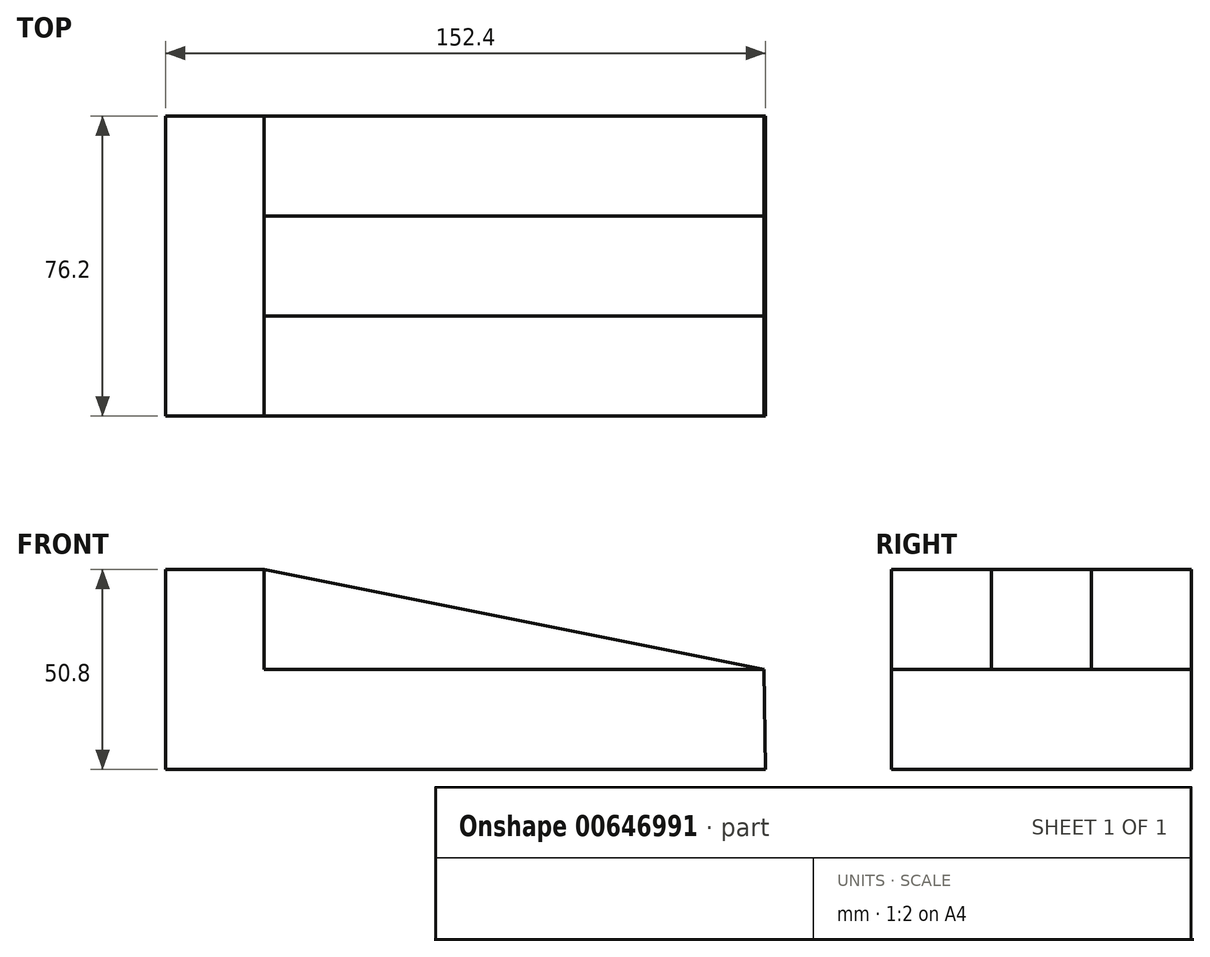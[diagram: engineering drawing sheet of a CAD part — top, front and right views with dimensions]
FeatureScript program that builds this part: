
annotation { "Feature Type Name" : "Feature", "Feature Type Description" : "" }
export const myFeature = defineFeature(function(context is Context, id is Id, definition is map)
    precondition{}
    {
        {
            var Q0;
            Q0=qCreatedBy(makeId("Front.planeOp"),FACE);
            var sketch = newSketch(context, id + "F0", { "sketchPlane" : qUnion([Q0])});
            skLineSegment(sketch, "E0", {"start": v(-56.03, 50.8) * mm, "end": v(-81.43, 50.8) * mm});
            skLineSegment(sketch, "E1", {"start": v(-81, 50.8) * mm, "end": v(-81, 0) * mm});
            skLineSegment(sketch, "E2", {"start": v(-81, 0) * mm, "end": v(71.4, 0) * mm});
            skLineSegment(sketch, "E3", {"start": v(71.4, 0) * mm, "end": v(70.97, 25.4) * mm});
            skLineSegment(sketch, "E4", {"start": v(70.97, 25.4) * mm, "end": v(-56.03, 25.4) * mm});
            skLineSegment(sketch, "E5", {"start": v(-56.03, 25.4) * mm, "end": v(-56.03, 50.8) * mm});
            skLineSegment(sketch, "E6", {"start": v(-56.03, 50.8) * mm, "end": v(70.97, 25.4) * mm});
            skSolve(sketch);
        }
        {
            var Q0;
            {var subQ0=sQuery(id+"F0.wireOp",EDGE,"E2");Q0=makeQuery(id+"F0.imprint","IMPRINT",FACE,{"disambiguationData":[TD([[makeQuery(id+"F0.imprint","IMPRINT",EDGE,{"derivedFrom":subQ0}),1.0]])]});}
            extrude(context, id + "F1", {"entities" : qUnion([Q0]), "depth" : 50.8 * mm, "offsetDistance" : 25.4 * mm, "hasSecondDirection" : true, "secondDirectionOppositeDirection" : true, "secondDirectionDepth" : 25.4 * mm});
        }
        {
            var Q0;
            Q0=makeQuery(id+"F0.imprint","IMPRINT",FACE,{"disambiguationData":[TD([[makeQuery(id+"F0.imprint","IMPRINT",EDGE,{"derivedFrom":sQuery(id+"F0.wireOp",EDGE,"E4")}),-1.0]])]});
            extrude(context, id + "F2", {"entities" : qUnion([Q0]), "operationType" : NewBodyOperationType.ADD, "depth" : 25.4 * mm, "offsetDistance" : 25.4 * mm});
        }
    });
